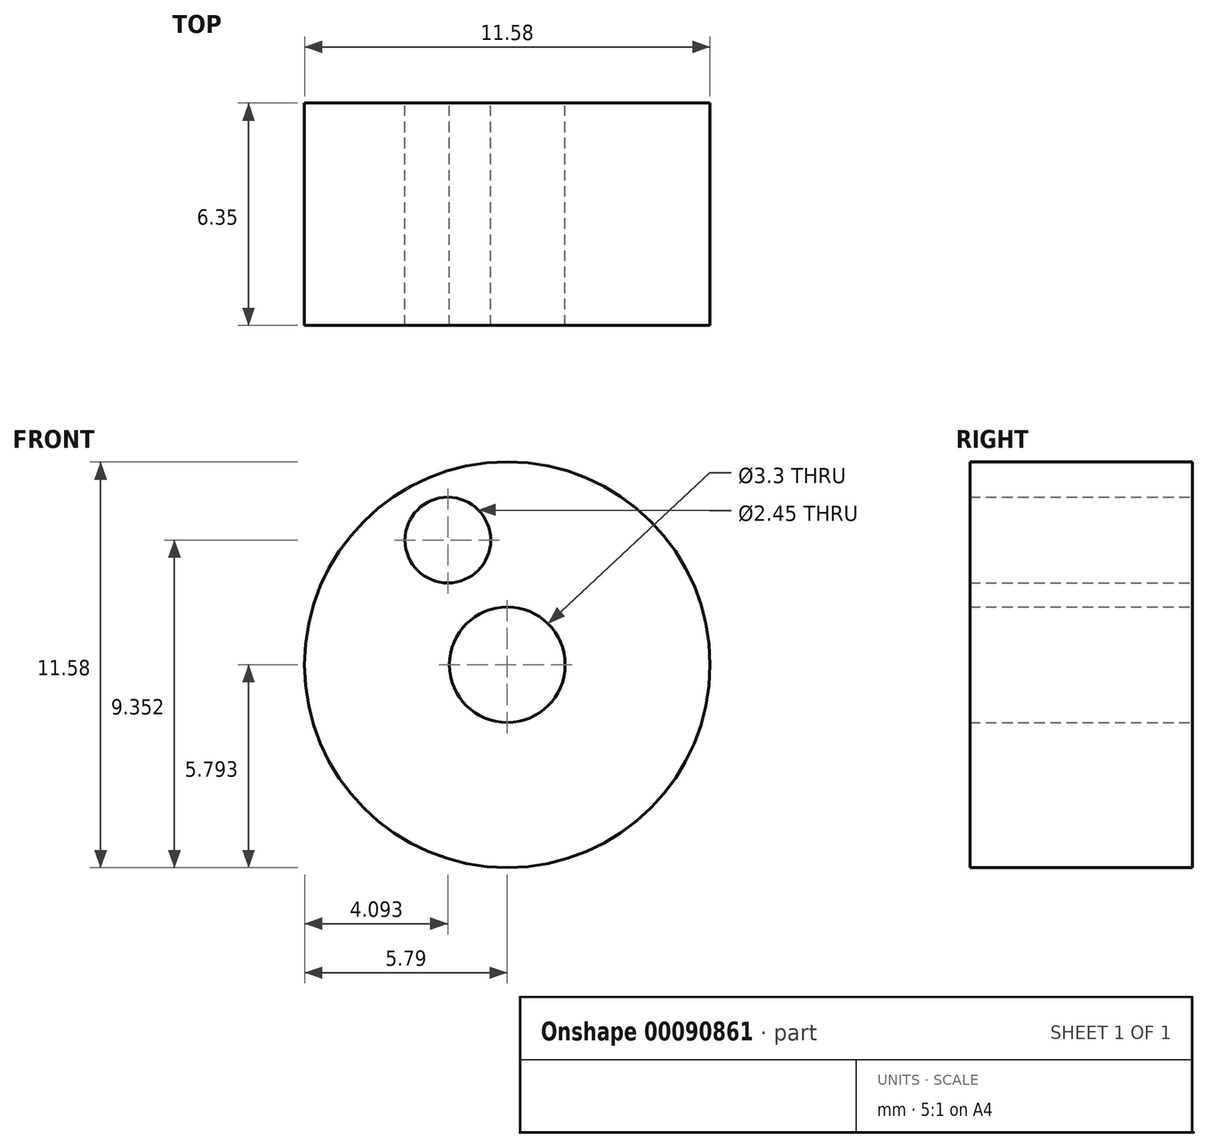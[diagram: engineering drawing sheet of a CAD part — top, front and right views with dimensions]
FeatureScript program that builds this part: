
annotation { "Feature Type Name" : "Feature", "Feature Type Description" : "" }
export const myFeature = defineFeature(function(context is Context, id is Id, definition is map)
    precondition{}
    {
        {
            var Q0;
            Q0=qCreatedBy(makeId("Front.planeOp"),FACE);
            var sketch = newSketch(context, id + "F0", { "sketchPlane" : qUnion([Q0])});
            skCircle(sketch, "E0", {"center": v(-32.2, 37.06) * mm, "radius": 5.8 * mm});
            skCircle(sketch, "E1", {"center": v(-32.2, 37.06) * mm, "radius": 1.65 * mm});
            skCircle(sketch, "E2", {"center": v(-33.9, 40.62) * mm, "radius": 1.22 * mm});
            skSolve(sketch);
        }
        {
            var Q0;
            Q0=makeQuery(id+"F0.imprint","IMPRINT",FACE,{"disambiguationData":[TD([[makeQuery(id+"F0.imprint","IMPRINT",EDGE,{"derivedFrom":sQuery(id+"F0.wireOp",EDGE,"E0")}),1.0]])]});
            extrude(context, id + "F1", {"entities" : qUnion([Q0]), "depth" : 6.35 * mm});
        }
    });
